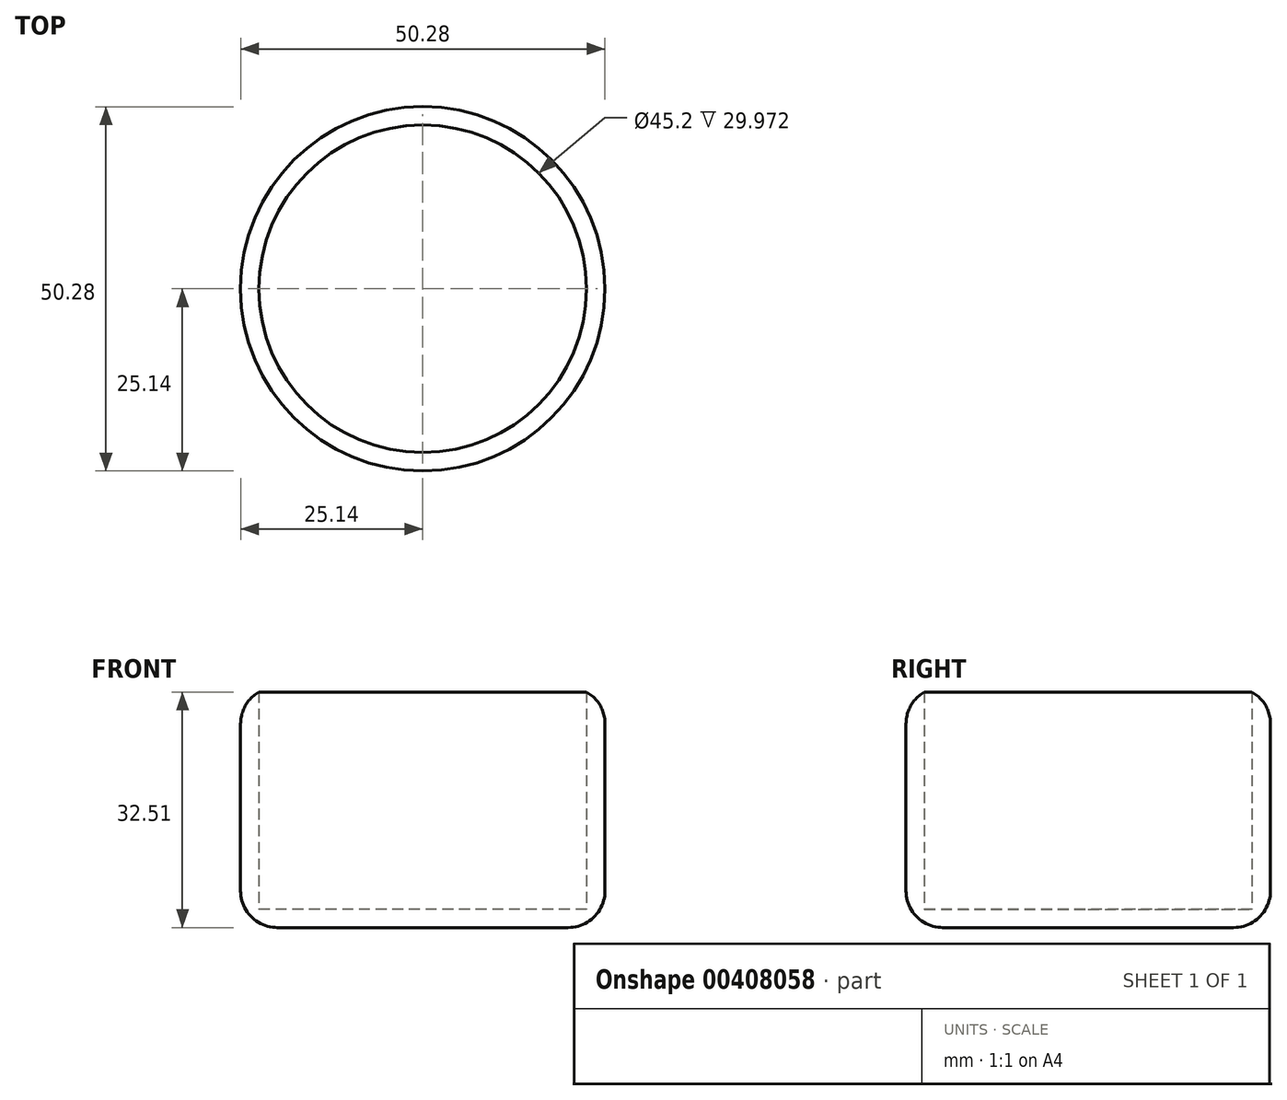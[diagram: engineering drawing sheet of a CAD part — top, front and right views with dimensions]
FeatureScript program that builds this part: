
annotation { "Feature Type Name" : "Feature", "Feature Type Description" : "" }
export const myFeature = defineFeature(function(context is Context, id is Id, definition is map)
    precondition{}
    {
        {
            var Q0;
            Q0=qCreatedBy(makeId("Top.planeOp"),FACE);
            var sketch = newSketch(context, id + "F0", { "sketchPlane" : qUnion([Q0])});
            skCircle(sketch, "E0", {"center": v(0, 0) * mm, "radius": 25.14 * mm});
            skSolve(sketch);
        }
        {
            var Q0;
            Q0 = qSketchRegion(id + "F0", true);
            extrude(context, id + "F1", {"entities" : qUnion([Q0]), "depth" : 32.5 * mm});
        }
        {
            var Q0;
            Q0=makeQuery(id+"F1.opExtrude","CAP_FACE",FACE,{"disambiguationData":[OSD([sQuery(id+"F0.wireOp",EDGE,"E0")])],"isStart":false});
            shell(context, id + "F2", {"entities" : qUnion([Q0]), "thickness" : 2.54 * mm});
        }
        {
            var Q0;
            Q0=makeQuery(id+"F1.opExtrude","CAP_EDGE",EDGE,{"disambiguationData":[OSD([sQuery(id+"F0.wireOp",EDGE,"E0")])],"isStart":false});
            var Q1;
            Q1=makeQuery(id+"F1.opExtrude","SWEPT_FACE",FACE,{"disambiguationData":[OSD([sQuery(id+"F0.wireOp",EDGE,"E0")])]});
            var Q2;
            Q2=makeQuery(id+"F1.opExtrude","CAP_EDGE",EDGE,{"disambiguationData":[OSD([sQuery(id+"F0.wireOp",EDGE,"E0")])],"isStart":true});
            fillet(context, id + "F3", {"entities" : qUnion([Q0, Q1, Q2]), "radius" : 5.08 * mm, "tangentPropagation" : true, "allowEdgeOverflow" : false});
        }
    });
